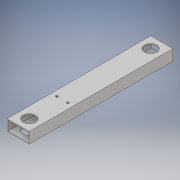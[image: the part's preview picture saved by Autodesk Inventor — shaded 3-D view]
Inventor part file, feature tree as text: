
AUTODESK INVENTOR PART (.ipt)
format: ipt  version: 2018 (Build 220112000, 112)  size: 126,464 bytes
history: native  units: in
note: dims shown in document units (in); Inventor stores cm internally (conversion verified against a paired STEP export)
features: extrude x2, sketch x2
ambient origin geometry x8: Origin, YZ Plane, XZ Plane, XY Plane, X Axis, Y Axis, Z Axis, Center Point
bodies: Solid1 (feature_tree)
feature tree (4):
  extrude  "Extrusion1"  Depth=1.0in
  extrude  "Extrusion2"  Depth=13.0in TaperAngle=0.0deg
  sketch  "Sketch1"  dims[d0=2.0in d1=1.0in]
  sketch  "Sketch2"  dims[d2=0.075in d3=13.0in d4=0.0in d5=1.0in d6=3.0in d7=1.0in d8=1.124in d9=1.125in d10=0.5in d11=0.5in d12=0.2031in d13=0.2031in d14=14.0in d15=0.0in]
